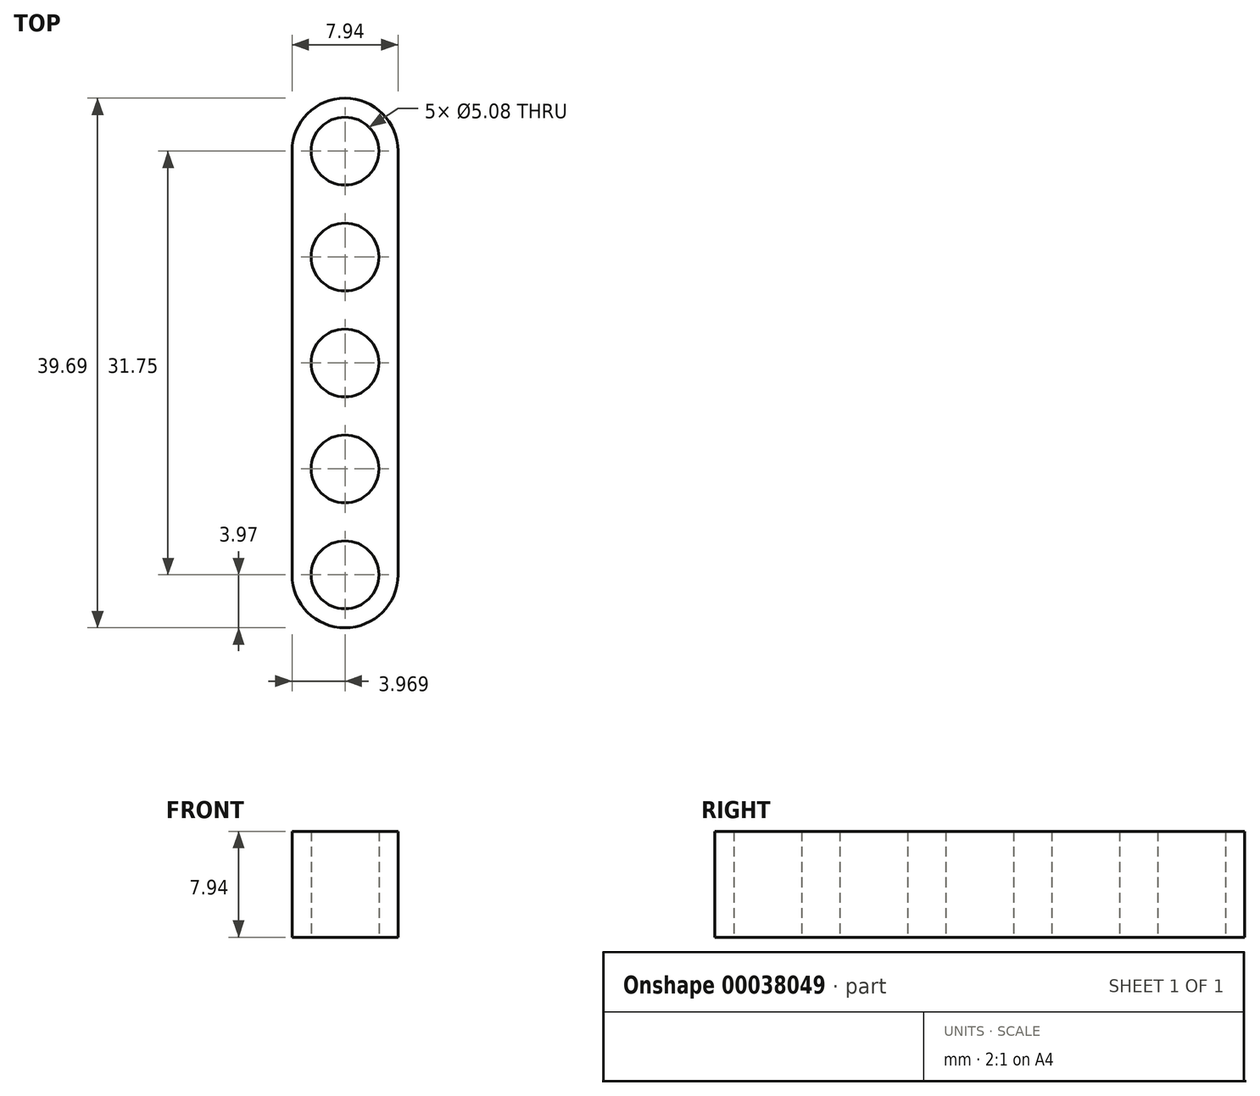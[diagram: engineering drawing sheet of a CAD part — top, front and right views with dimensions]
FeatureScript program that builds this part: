
annotation { "Feature Type Name" : "Feature", "Feature Type Description" : "" }
export const myFeature = defineFeature(function(context is Context, id is Id, definition is map)
    precondition{}
    {
        {
            var Q0;
            Q0=qCreatedBy(makeId("Top.planeOp"),FACE);
            var sketch = newSketch(context, id + "F0", { "sketchPlane" : qUnion([Q0])});
            skLineSegment(sketch, "E0.bottom", {"start": v(0, 0) * mm, "end": v(7.94, 0) * mm, "construction": true});
            skLineSegment(sketch, "E0.top", {"start": v(0, -31.75) * mm, "end": v(7.94, -31.75) * mm, "construction": true});
            skLineSegment(sketch, "E0.left", {"start": v(0, 0) * mm, "end": v(0, -31.75) * mm});
            skLineSegment(sketch, "E0.right", {"start": v(7.94, 0) * mm, "end": v(7.94, -31.75) * mm});
            skLineSegment(sketch, "E1", {"start": v(3.97, 0) * mm, "end": v(3.97, -7.94) * mm, "construction": true});
            skLineSegment(sketch, "E2", {"start": v(3.97, -7.94) * mm, "end": v(3.97, -15.88) * mm, "construction": true});
            skLineSegment(sketch, "E3", {"start": v(3.97, -15.88) * mm, "end": v(3.97, -23.81) * mm, "construction": true});
            skLineSegment(sketch, "E4", {"start": v(3.97, -23.81) * mm, "end": v(3.97, -31.75) * mm, "construction": true});
            skArc(sketch, "E5", {"start": v(7.94, 0) * mm, "mid": v(3.97, 3.97) * mm, "end": v(0, 0) * mm});
            skArc(sketch, "E6", {"start": v(0, -31.75) * mm, "mid": v(3.97, -35.72) * mm, "end": v(7.94, -31.75) * mm});
            skCircle(sketch, "E7", {"center": v(3.97, 0) * mm, "radius": 2.54 * mm});
            skCircle(sketch, "E8", {"center": v(3.97, -7.94) * mm, "radius": 2.54 * mm});
            skCircle(sketch, "E9", {"center": v(3.97, -15.88) * mm, "radius": 2.54 * mm});
            skCircle(sketch, "E10", {"center": v(3.97, -23.81) * mm, "radius": 2.54 * mm});
            skCircle(sketch, "E11", {"center": v(3.97, -31.75) * mm, "radius": 2.54 * mm});
            skSolve(sketch);
        }
        {
            var Q0;
            Q0 = qSketchRegion(id + "F0", true);
            extrude(context, id + "F1", {"entities" : qUnion([Q0]), "depth" : 7.94 * mm});
        }
    });
